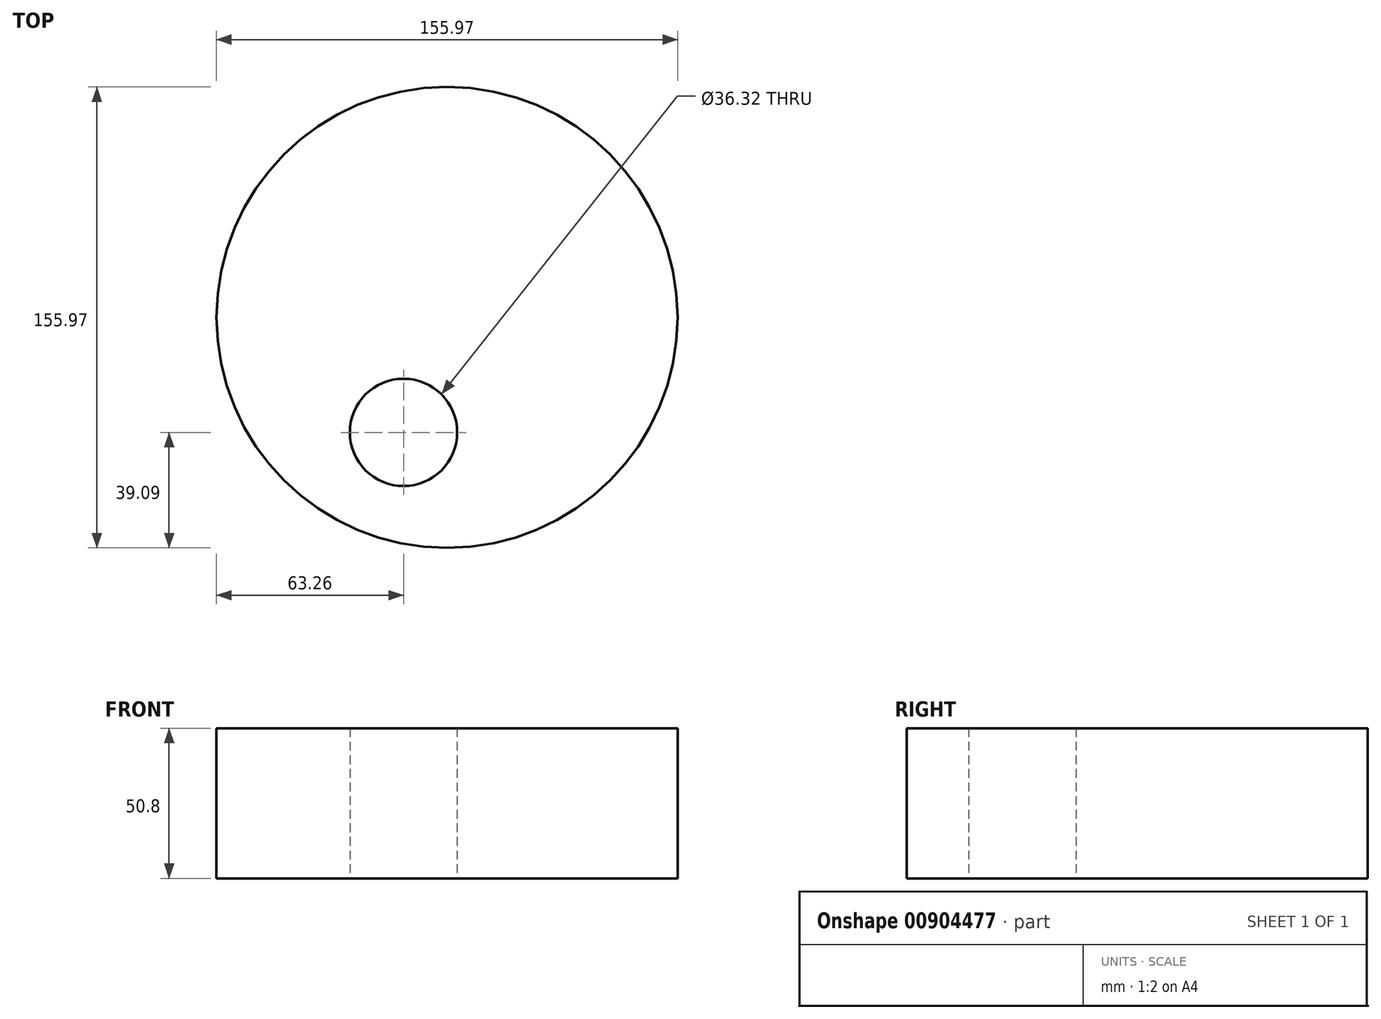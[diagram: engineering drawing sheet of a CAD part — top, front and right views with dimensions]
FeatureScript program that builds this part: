
annotation { "Feature Type Name" : "Feature", "Feature Type Description" : "" }
export const myFeature = defineFeature(function(context is Context, id is Id, definition is map)
    precondition{}
    {
        {
            var Q0;
            Q0=qCreatedBy(makeId("Top.planeOp"),FACE);
            var sketch = newSketch(context, id + "F0", { "sketchPlane" : qUnion([Q0])});
            skCircle(sketch, "E0", {"center": v(14.73, 38.9) * mm, "radius": 77.98 * mm});
            skCircle(sketch, "E1", {"center": v(0, 0) * mm, "radius": 18.16 * mm});
            skSolve(sketch);
        }
        {
            var Q0;
            Q0=makeQuery(id+"F0.imprint","IMPRINT",FACE,{"disambiguationData":[TD([[makeQuery(id+"F0.imprint","IMPRINT",EDGE,{"derivedFrom":sQuery(id+"F0.wireOp",EDGE,"E0")}),1.0]])]});
            extrude(context, id + "F1", {"entities" : qUnion([Q0]), "depth" : 50.8 * mm, "offsetDistance" : 25.4 * mm});
        }
    });
